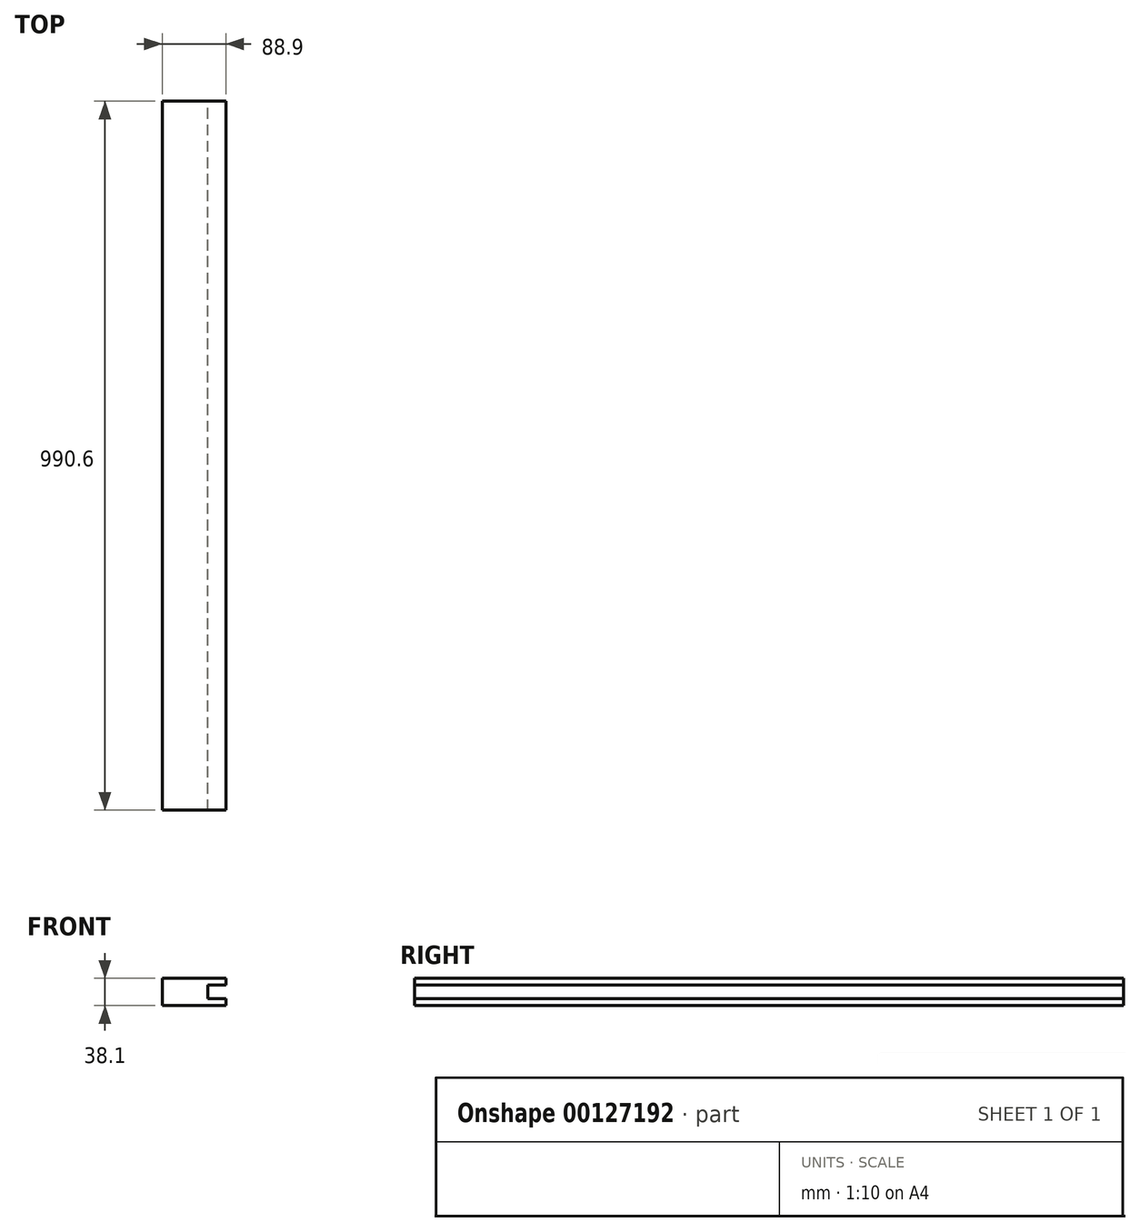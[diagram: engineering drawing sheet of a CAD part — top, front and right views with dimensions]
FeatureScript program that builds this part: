
annotation { "Feature Type Name" : "Feature", "Feature Type Description" : "" }
export const myFeature = defineFeature(function(context is Context, id is Id, definition is map)
    precondition{}
    {
        {
            var Q0;
            Q0=qCreatedBy(makeId("Front.planeOp"),FACE);
            var sketch = newSketch(context, id + "F0", { "sketchPlane" : qUnion([Q0])});
            skLineSegment(sketch, "E0.bottom", {"start": v(44.45, -19.05) * mm, "end": v(-44.45, -19.05) * mm});
            skLineSegment(sketch, "E0.top", {"start": v(44.45, 19.05) * mm, "end": v(-44.45, 19.05) * mm});
            skLineSegment(sketch, "E0.right", {"start": v(-44.45, -19.05) * mm, "end": v(-44.45, 19.05) * mm});
            skPoint(sketch, "E0.middle", {"position": v(0, 0) * mm});
            skLineSegment(sketch, "E1.top", {"start": v(44.45, -9.52) * mm, "end": v(19.05, -9.52) * mm});
            skLineSegment(sketch, "E1.right", {"start": v(19.05, 0) * mm, "end": v(19.05, -9.52) * mm});
            skLineSegment(sketch, "E2.top", {"start": v(44.45, 9.53) * mm, "end": v(19.05, 9.53) * mm});
            skLineSegment(sketch, "E2.right", {"start": v(19.05, 0) * mm, "end": v(19.05, 9.53) * mm});
            skLineSegment(sketch, "E3", {"start": v(44.45, 9.53) * mm, "end": v(44.45, 19.05) * mm});
            skLineSegment(sketch, "E4", {"start": v(44.45, -9.52) * mm, "end": v(44.45, -19.05) * mm});
            skSolve(sketch);
        }
        {
            var Q0;
            Q0=qSketchRegion(id+"F0",true);
            extrude(context, id + "F1", {"entities" : qUnion([Q0]), "depth" : 990.6 * mm});
        }
    });
